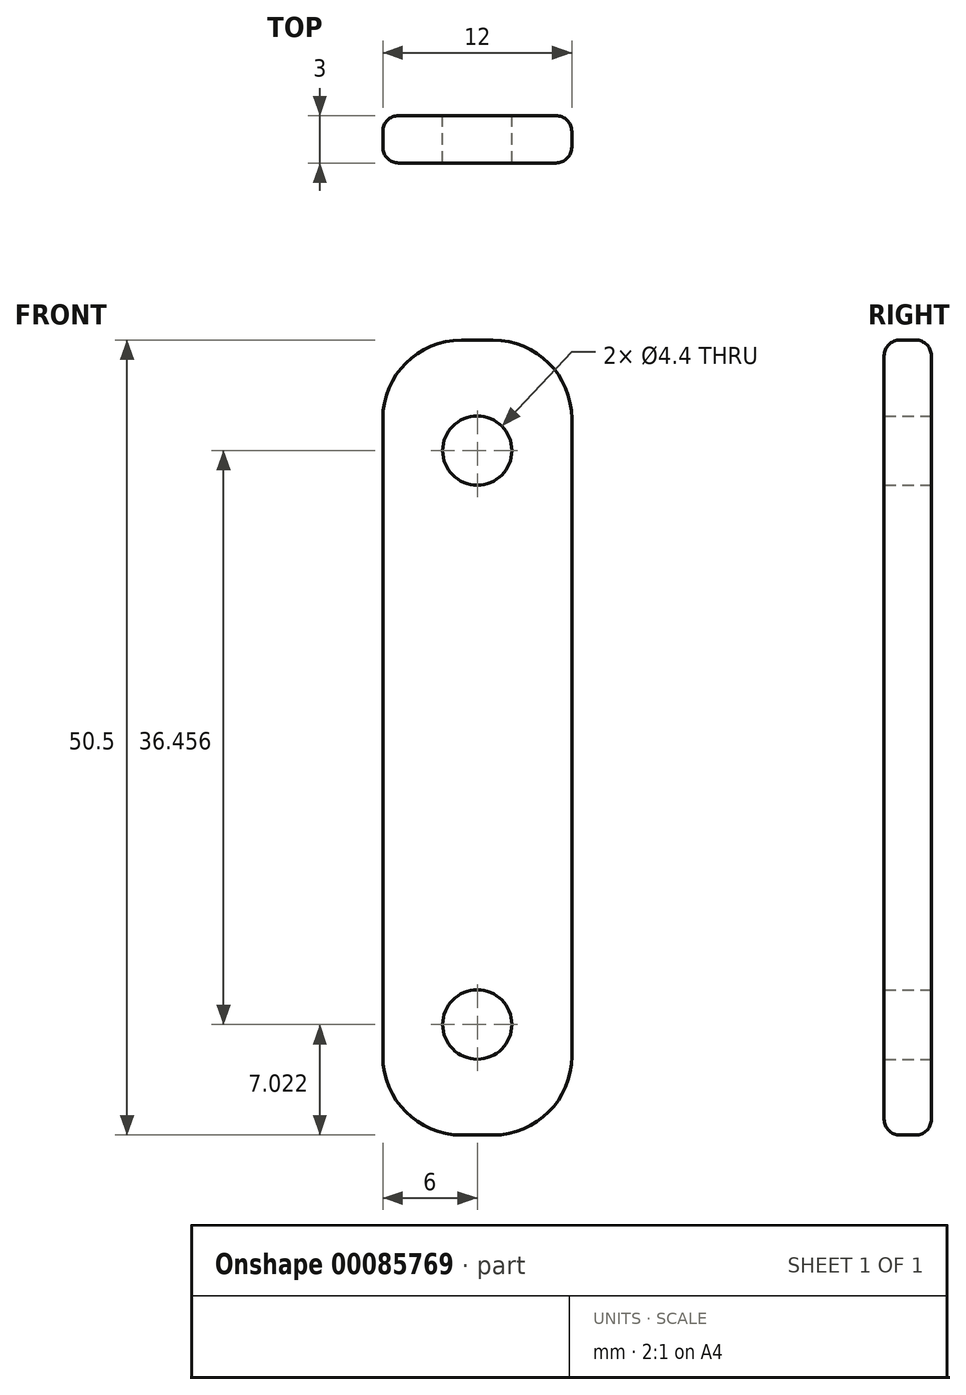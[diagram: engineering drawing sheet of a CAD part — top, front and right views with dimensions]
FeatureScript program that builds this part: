
annotation { "Feature Type Name" : "Feature", "Feature Type Description" : "" }
export const myFeature = defineFeature(function(context is Context, id is Id, definition is map)
    precondition{}
    {
        {
            var Q0;
            Q0=qCreatedBy(makeId("Front.planeOp"),FACE);
            var sketch = newSketch(context, id + "F0", { "sketchPlane" : qUnion([Q0])});
            skLineSegment(sketch, "E0.bottom", {"start": v(6, 25.25) * mm, "end": v(-6, 25.25) * mm});
            skLineSegment(sketch, "E0.top", {"start": v(6, -25.25) * mm, "end": v(-6, -25.25) * mm});
            skLineSegment(sketch, "E0.left", {"start": v(6, 25.25) * mm, "end": v(6, -25.25) * mm});
            skLineSegment(sketch, "E0.right", {"start": v(-6, 25.25) * mm, "end": v(-6, -25.25) * mm});
            skPoint(sketch, "E0.middle", {"position": v(0, 0) * mm});
            skSolve(sketch);
        }
        {
            var Q0;
            Q0=makeQuery(id+"F0.imprint","IMPRINT",FACE,{"disambiguationData":[TD([[makeQuery(id+"F0.imprint","IMPRINT",EDGE,{"derivedFrom":sQuery(id+"F0.wireOp",EDGE,"E0.bottom")}),1.0]])]});
            extrude(context, id + "F1", {"entities" : qUnion([Q0]), "depth" : 3 * mm});
        }
        {
            var Q0;
            Q0=qCreatedBy(makeId("Front.planeOp"),FACE);
            cPlane(context, id + "F2", {"entities" : qUnion([Q0]), "cplaneType" : CPlaneType.OFFSET, "offset" : 8 * mm, "oppositeDirection" : true, "width" : 150 * mm, "height" : 150 * mm});
        }
        {
            var Q0;
            Q0=qCreatedBy(id+"F2.planeOp",FACE);
            var sketch = newSketch(context, id + "F3", { "sketchPlane" : qUnion([Q0])});
            skPoint(sketch, "E1", {"position": v(0, 18.23) * mm});
            skPoint(sketch, "E2", {"position": v(0, -18.23) * mm});
            skSolve(sketch);
        }
        {
            var Q0;
            Q0=sQuery(id+"F3.wireOp",VERTEX,"E1");
            var Q1;
            Q1=sQuery(id+"F3.wireOp",VERTEX,"E2");
            var Q2;
            Q2=makeQuery(id+"F1.opExtrude","SWEPT_BODY",BODY,{"disambiguationData":[OSD([sQuery(id+"F0.wireOp",EDGE,"E0.bottom"),sQuery(id+"F0.wireOp",EDGE,"E0.top"),sQuery(id+"F0.wireOp",EDGE,"E0.left"),sQuery(id+"F0.wireOp",EDGE,"E0.right")])]});
            hole(context, id + "F4", {"style" : HoleStyle.C_BORE, "endStyle" : HoleEndStyle.BLIND, "oppositeDirection" : true, "holeDiameter" : 4.4 * mm, "cBoreDiameter" : 8.25 * mm, "cBoreDepth" : 4 * mm, "holeDepth" : 70 * mm, "startFromSketch" : true, "locations" : qUnion([Q0, Q1]), "scope" : qUnion([Q2])});
        }
        {
            var Q0;
            Q0=makeQuery(id+"F1.opExtrude","SWEPT_EDGE",EDGE,{"disambiguationData":[OSD([sQuery(id+"F0.wireOp",EDGE,"E0.bottom"),sQuery(id+"F0.wireOp",EDGE,"E0.right")])]});
            var Q1;
            Q1=makeQuery(id+"F1.opExtrude","SWEPT_EDGE",EDGE,{"disambiguationData":[OSD([sQuery(id+"F0.wireOp",EDGE,"E0.bottom"),sQuery(id+"F0.wireOp",EDGE,"E0.left")])]});
            var Q2;
            Q2=makeQuery(id+"F1.opExtrude","SWEPT_EDGE",EDGE,{"disambiguationData":[OSD([sQuery(id+"F0.wireOp",EDGE,"E0.top"),sQuery(id+"F0.wireOp",EDGE,"E0.right")])]});
            var Q3;
            Q3=makeQuery(id+"F1.opExtrude","SWEPT_EDGE",EDGE,{"disambiguationData":[OSD([sQuery(id+"F0.wireOp",EDGE,"E0.top"),sQuery(id+"F0.wireOp",EDGE,"E0.left")])]});
            fillet(context, id + "F5", {"entities" : qUnion([Q0, Q1, Q2, Q3]), "radius" : 5 * mm, "tangentPropagation" : true, "allowEdgeOverflow" : false});
        }
        {
            var Q0;
            Q0=makeQuery(id+"F1.opExtrude","CAP_EDGE",EDGE,{"disambiguationData":[OSD([sQuery(id+"F0.wireOp",EDGE,"E0.left")])],"isStart":true});
            var Q1;
            Q1=makeQuery(id+"F1.opExtrude","CAP_EDGE",EDGE,{"disambiguationData":[OSD([sQuery(id+"F0.wireOp",EDGE,"E0.left")])],"isStart":false});
            fillet(context, id + "F6", {"entities" : qUnion([Q0, Q1]), "radius" : 1 * mm, "tangentPropagation" : true, "allowEdgeOverflow" : false});
        }
    });
